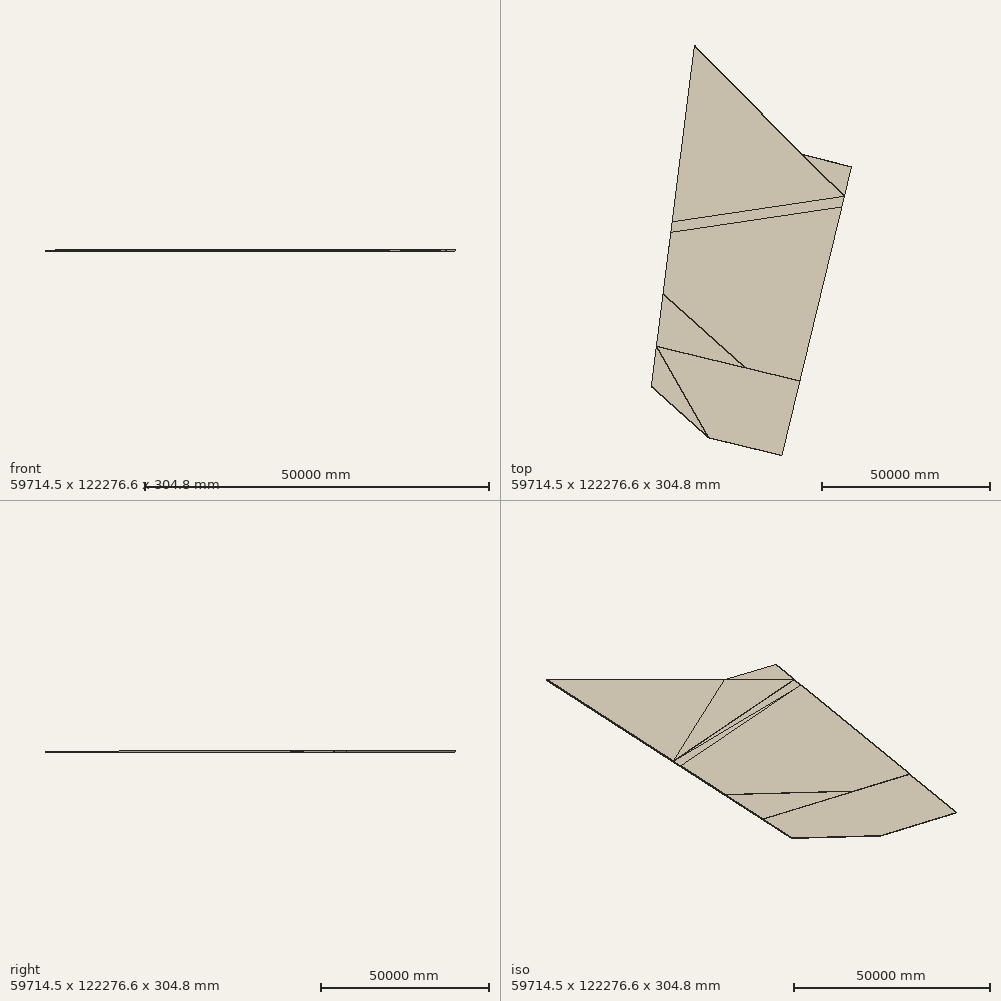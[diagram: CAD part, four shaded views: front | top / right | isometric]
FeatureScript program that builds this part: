
annotation { "Feature Type Name" : "Feature", "Feature Type Description" : "" }
export const myFeature = defineFeature(function(context is Context, id is Id, definition is map)
    precondition{}
    {
        {
            var Q0;
            Q0=qCreatedBy(makeId("Top.planeOp"),FACE);
            var sketch = newSketch(context, id + "F0", { "sketchPlane" : qUnion([Q0])});
            skLineSegment(sketch, "E0", {"start": v(0, 0) * mm, "end": v(31989.83, -32467.96) * mm});
            skLineSegment(sketch, "E1", {"start": v(31989.83, -32467.96) * mm, "end": v(46862.18, -36229.17) * mm});
            skLineSegment(sketch, "E2", {"start": v(46862.18, -36229.17) * mm, "end": v(26112.23, -122276.56) * mm});
            skLineSegment(sketch, "E3", {"start": v(46862.18, -36229.17) * mm, "end": v(46862.18, -51469.17) * mm, "construction": true});
            skLineSegment(sketch, "E4", {"start": v(0, 0) * mm, "end": v(-12852.3, -101676.89) * mm});
            skLineSegment(sketch, "E5", {"start": v(0, 0) * mm, "end": v(0, 15240) * mm, "construction": true});
            skLineSegment(sketch, "E6", {"start": v(26112.23, -122276.56) * mm, "end": v(4230, -116999.76) * mm});
            skLineSegment(sketch, "E7", {"start": v(26112.23, -122276.56) * mm, "end": v(10872.23, -122276.56) * mm, "construction": true});
            skLineSegment(sketch, "E8", {"start": v(4230, -116999.76) * mm, "end": v(-12852.3, -101676.89) * mm});
            skArc(sketch, "E9", {"start": v(-4165.07, -109469.35) * mm, "mid": v(-689.73, -114039.67) * mm, "end": v(4230, -116999.76) * mm, "construction": true});
            skArc(sketch, "E10", {"start": v(-4165.07, -109469.35) * mm, "mid": v(-8132.26, -105153.47) * mm, "end": v(-12852.3, -101676.89) * mm, "construction": true});
            skLineSegment(sketch, "E11", {"start": v(31471.2, -100053.58) * mm, "end": v(-11342.08, -89729.35) * mm});
            skLineSegment(sketch, "E12", {"start": v(-9365.85, -74095.03) * mm, "end": v(15198.72, -96129.54) * mm});
            skLineSegment(sketch, "E13", {"start": v(-6651.63, -52622.31) * mm, "end": v(44754.67, -44968.73) * mm});
            skLineSegment(sketch, "E14", {"start": v(-7048.63, -55763.02) * mm, "end": v(43983.88, -48165.09) * mm});
            skSolve(sketch);
        }
        {
            var Q0;
            {var subQ4=sQuery(id+"F0.wireOp",EDGE,"E0");Q0=makeQuery(id+"F0.imprint","IMPRINT",FACE,{"disambiguationData":[TD([[makeQuery(id+"F0.imprint","IMPRINT",EDGE,{"derivedFrom":subQ4}),-1.0]])]});}
            var Q1;
            {var subQ0=sQuery(id+"F0.wireOp",EDGE,"E13");Q1=makeQuery(id+"F0.imprint","IMPRINT",FACE,{"disambiguationData":[TD([[makeQuery(id+"F0.imprint","IMPRINT",EDGE,{"derivedFrom":subQ0}),-1.0]])]});}
            var Q2;
            {var subQ0=sQuery(id+"F0.wireOp",EDGE,"E12");Q2=makeQuery(id+"F0.imprint","IMPRINT",FACE,{"disambiguationData":[TD([[makeQuery(id+"F0.imprint","IMPRINT",EDGE,{"derivedFrom":subQ0}),1.0]])]});}
            var Q3;
            {var subQ3=sQuery(id+"F0.wireOp",EDGE,"E12");Q3=makeQuery(id+"F0.imprint","IMPRINT",FACE,{"disambiguationData":[TD([[makeQuery(id+"F0.imprint","IMPRINT",EDGE,{"derivedFrom":subQ3}),-1.0]])]});}
            var Q4;
            {var subQ1=sQuery(id+"F0.wireOp",EDGE,"E6");Q4=makeQuery(id+"F0.imprint","IMPRINT",FACE,{"disambiguationData":[TD([[makeQuery(id+"F0.imprint","IMPRINT",EDGE,{"derivedFrom":subQ1}),-1.0]])]});}
            extrude(context, id + "F1", {"entities" : qUnion([Q0, Q1, Q2, Q3, Q4]), "depth" : 304.8 * mm, "offsetDistance" : 25.4 * mm});
        }
        {
            var Q0;
            Q0=makeQuery(id+"F1.opExtrude","CAP_FACE",FACE,{"disambiguationData":[OSD([sQuery(id+"F0.wireOp",EDGE,"E0"),sQuery(id+"F0.wireOp",EDGE,"E1"),sQuery(id+"F0.wireOp",EDGE,"E2"),sQuery(id+"F0.wireOp",EDGE,"E4"),sQuery(id+"F0.wireOp",EDGE,"E6"),sQuery(id+"F0.wireOp",EDGE,"E8")])],"isStart":false});
            var sketch = newSketch(context, id + "F2", { "sketchPlane" : qUnion([Q0])});
            skLineSegment(sketch, "E15.0", {"start": v(-9365.85, -74095.03) * mm, "end": v(15198.72, -96129.54) * mm});
            skLineSegment(sketch, "E16.0", {"start": v(31471.2, -100053.58) * mm, "end": v(-11342.08, -89729.35) * mm});
            skLineSegment(sketch, "E17.0", {"start": v(0, 0) * mm, "end": v(-12852.3, -101676.89) * mm});
            skSolve(sketch);
        }
        {
            var Q0;
            {var subQ0=sQuery(id+"F2.wireOp",EDGE,"E15.0");Q0=makeQuery(id+"F2.imprint","IMPRINT",FACE,{"disambiguationData":[TD([[makeQuery(id+"F2.imprint","IMPRINT",EDGE,{"derivedFrom":subQ0}),-1.0]])]});}
            extrude(context, id + "F3", {"entities" : qUnion([Q0]), "operationType" : NewBodyOperationType.REMOVE, "oppositeDirection" : true, "depth" : 76.2 * mm, "offsetDistance" : 25.4 * mm});
        }
        {
            var Q0;
            Q0=makeQuery(id+"F1.opExtrude","CAP_FACE",FACE,{"disambiguationData":[OSD([sQuery(id+"F0.wireOp",EDGE,"E0"),sQuery(id+"F0.wireOp",EDGE,"E1"),sQuery(id+"F0.wireOp",EDGE,"E2"),sQuery(id+"F0.wireOp",EDGE,"E4"),sQuery(id+"F0.wireOp",EDGE,"E6"),sQuery(id+"F0.wireOp",EDGE,"E8")])],"isStart":false});
            var sketch = newSketch(context, id + "F4", { "sketchPlane" : qUnion([Q0])});
            skLineSegment(sketch, "E18.0", {"start": v(0, 0) * mm, "end": v(-12852.3, -101676.89) * mm});
            skLineSegment(sketch, "E19.0", {"start": v(4230, -116999.76) * mm, "end": v(-12852.3, -101676.89) * mm});
            skLineSegment(sketch, "E20.0", {"start": v(26112.23, -122276.56) * mm, "end": v(4230, -116999.76) * mm});
            skLineSegment(sketch, "E21.0", {"start": v(46862.18, -36229.17) * mm, "end": v(26112.23, -122276.56) * mm});
            skLineSegment(sketch, "E22.0", {"start": v(31471.2, -100053.58) * mm, "end": v(-11342.08, -89729.35) * mm});
            skSolve(sketch);
        }
        {
            var Q0;
            {var subQ4=sQuery(id+"F4.wireOp",EDGE,"E19.0");Q0=makeQuery(id+"F4.imprint","IMPRINT",FACE,{"disambiguationData":[TD([[makeQuery(id+"F4.imprint","IMPRINT",EDGE,{"derivedFrom":subQ4}),-1.0]])]});}
            extrude(context, id + "F5", {"entities" : qUnion([Q0]), "operationType" : NewBodyOperationType.REMOVE, "oppositeDirection" : true, "depth" : 152.4 * mm, "offsetDistance" : 25.4 * mm});
        }
        {
            var Q0;
            Q0=makeQuery(id+"F1.opExtrude","CAP_FACE",FACE,{"disambiguationData":[OSD([sQuery(id+"F0.wireOp",EDGE,"E0"),sQuery(id+"F0.wireOp",EDGE,"E1"),sQuery(id+"F0.wireOp",EDGE,"E2"),sQuery(id+"F0.wireOp",EDGE,"E4"),sQuery(id+"F0.wireOp",EDGE,"E6"),sQuery(id+"F0.wireOp",EDGE,"E8")])],"isStart":false});
            var sketch = newSketch(context, id + "F6", { "sketchPlane" : qUnion([Q0])});
            skLineSegment(sketch, "E23.0", {"start": v(-6651.63, -52622.31) * mm, "end": v(44754.67, -44968.73) * mm});
            skLineSegment(sketch, "E24.0", {"start": v(-7048.63, -55763.02) * mm, "end": v(43983.88, -48165.09) * mm});
            skLineSegment(sketch, "E25.0", {"start": v(0, 0) * mm, "end": v(-12852.3, -101676.89) * mm});
            skLineSegment(sketch, "E26.0", {"start": v(46862.18, -36229.17) * mm, "end": v(26112.23, -122276.56) * mm});
            skSolve(sketch);
        }
        {
            var Q0;
            {var subQ0=sQuery(id+"F6.wireOp",EDGE,"E23.0");Q0=makeQuery(id+"F6.imprint","IMPRINT",FACE,{"disambiguationData":[TD([[makeQuery(id+"F6.imprint","IMPRINT",EDGE,{"derivedFrom":subQ0}),-1.0]])]});}
            extrude(context, id + "F7", {"entities" : qUnion([Q0]), "operationType" : NewBodyOperationType.REMOVE, "oppositeDirection" : true, "depth" : 152.4 * mm, "offsetDistance" : 25.4 * mm});
        }
    });
